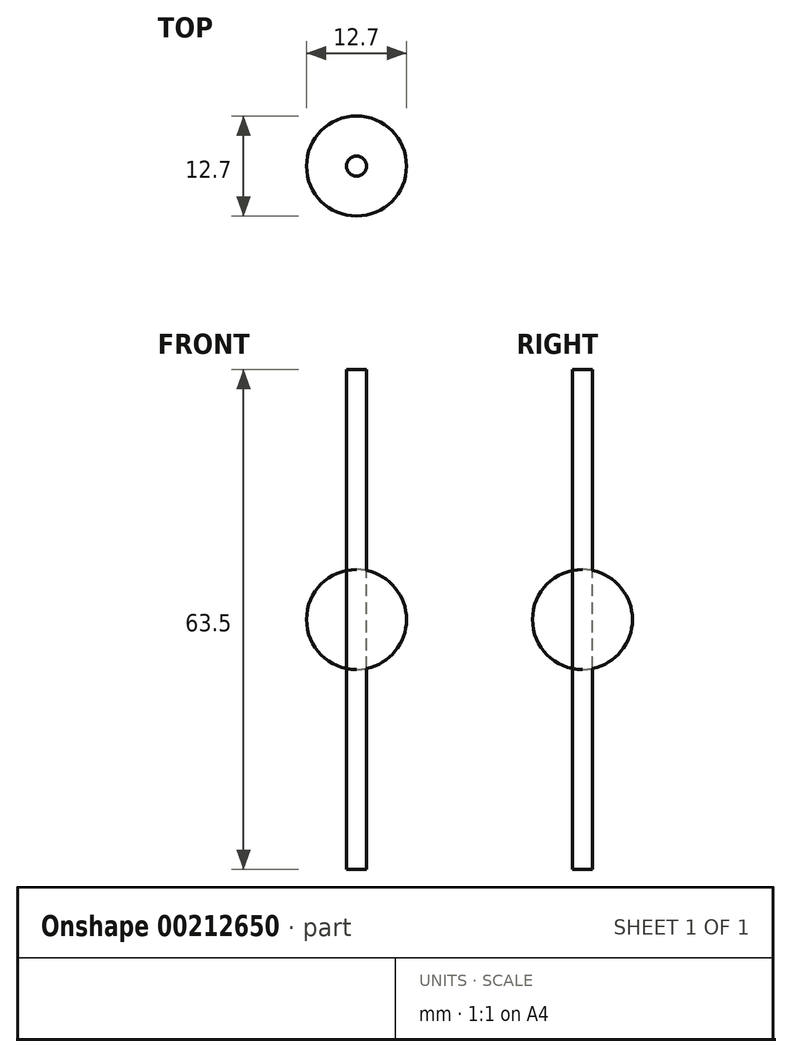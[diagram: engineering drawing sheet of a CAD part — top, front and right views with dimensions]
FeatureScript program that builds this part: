
annotation { "Feature Type Name" : "Feature", "Feature Type Description" : "" }
export const myFeature = defineFeature(function(context is Context, id is Id, definition is map)
    precondition{}
    {
        {
            var Q0;
            Q0=qCreatedBy(makeId("Front.planeOp"),FACE);
            var sketch = newSketch(context, id + "F0", { "sketchPlane" : qUnion([Q0])});
            skArc(sketch, "E0", {"start": v(0, 12.7) * mm, "mid": v(-6.35, 6.35) * mm, "end": v(0, 0) * mm});
            skLineSegment(sketch, "E1", {"start": v(0, 12.7) * mm, "end": v(0, 17.9) * mm});
            skSolve(sketch);
        }
        {
            var Q0;
            Q0=sQuery(id+"F0.wireOp",EDGE,"E0");
            var Q1;
            Q1=sQuery(id+"F0.wireOp",EDGE,"E1");
            revolve(context, id + "F1", {"bodyType" : ToolBodyType.SURFACE, "surfaceEntities" : qUnion([Q0]), "axis" : qUnion([Q1]), "revolveType" : RevolveType.FULL});
        }
        {
            var Q0;
            Q0=qCreatedBy(makeId("Top.planeOp"),FACE);
            var sketch = newSketch(context, id + "F2", { "sketchPlane" : qUnion([Q0])});
            skCircle(sketch, "E2", {"center": v(0, 0) * mm, "radius": 1.27 * mm});
            skSolve(sketch);
        }
        {
            var Q0;
            Q0=sQuery(id+"F2.wireOp",EDGE,"E2");
            extrude(context, id + "F3", {"bodyType" : ToolBodyType.SURFACE, "surfaceEntities" : qUnion([Q0]), "depth" : 38.1 * mm, "hasSecondDirection" : true, "secondDirectionOppositeDirection" : true, "secondDirectionDepth" : 25.4 * mm});
        }
    });
